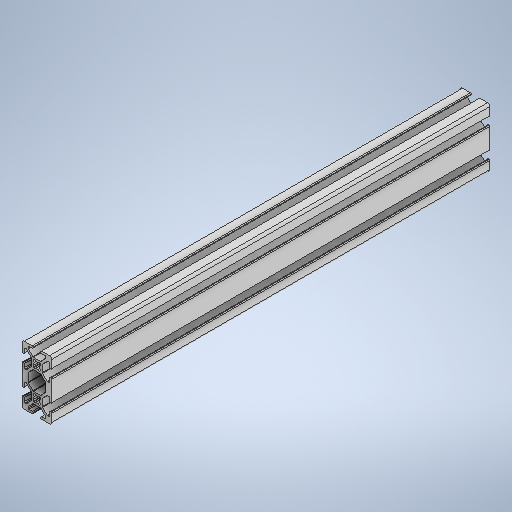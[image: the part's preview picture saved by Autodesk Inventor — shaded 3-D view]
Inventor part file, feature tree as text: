
AUTODESK INVENTOR PART (.ipt)
format: ipt  version: 2025 (Build 290162000, 162)  size: 483,840 bytes
history: native  units: in
note: dims shown in document units (in); Inventor stores cm internally (conversion verified against a paired STEP export)
features: extrude x1, sketch x1
ambient origin geometry x8: Origin, YZ Plane, XZ Plane, XY Plane, X Axis, Y Axis, Z Axis, Center Point
bodies: Solid1 (feature_tree)
feature tree (2):
  extrude  "Extrusion1"  [1 undecoded]
  sketch  "Sketch1"  dims[d0=11.7in d1=0.0in]
note: 1 required parameter value undecoded (feature->parameter linkage not recoverable at this tier; creation-order binding heuristic only, values carry confidence <= 0.55)
